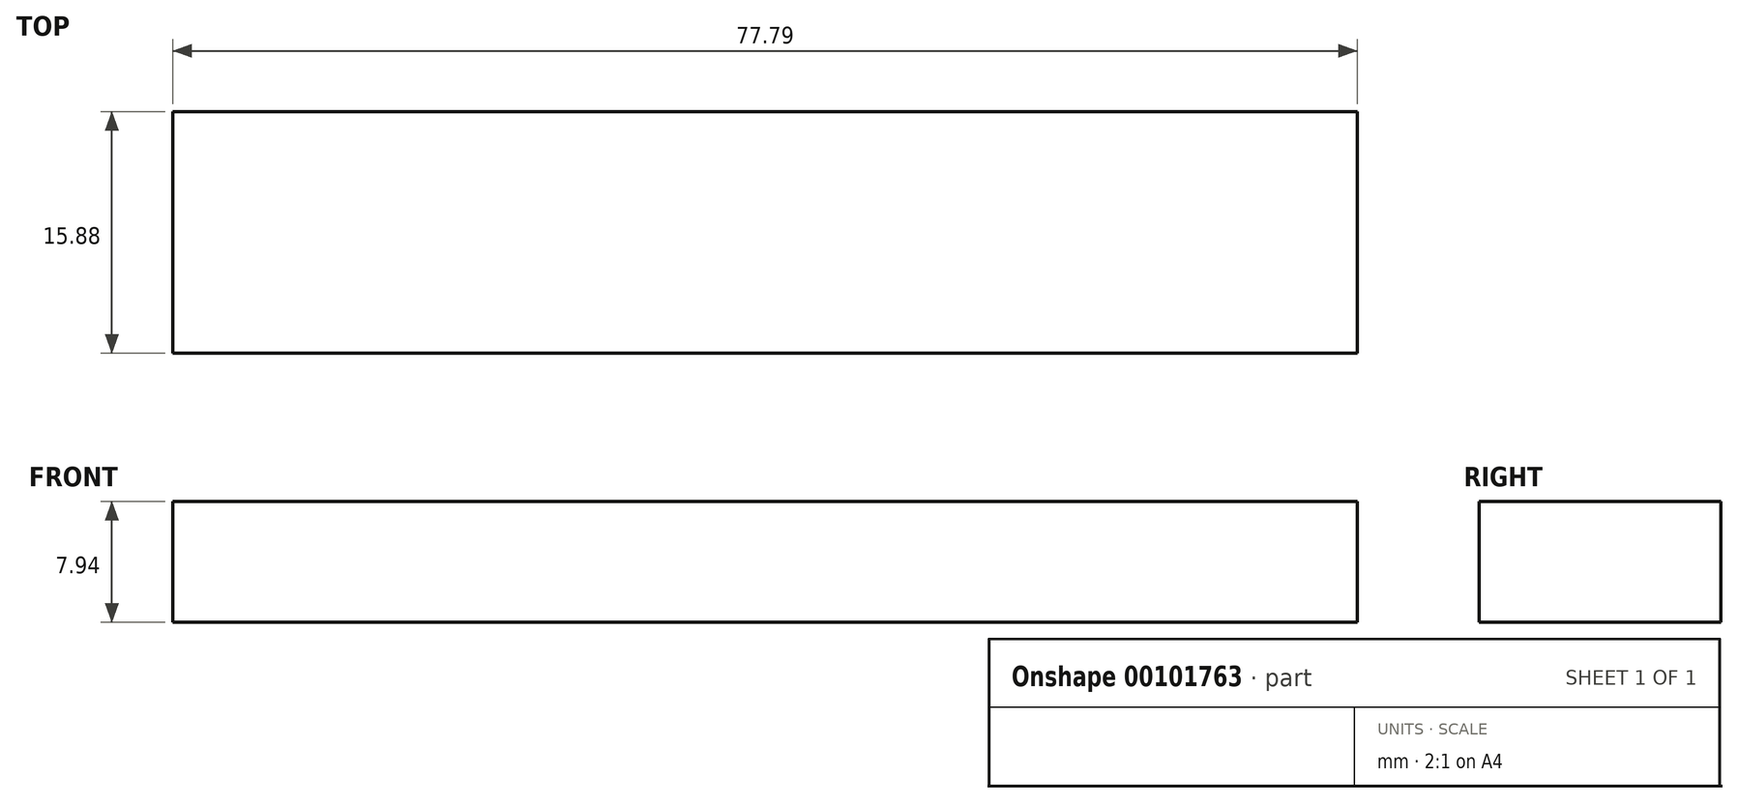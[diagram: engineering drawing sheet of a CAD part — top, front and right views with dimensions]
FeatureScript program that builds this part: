
annotation { "Feature Type Name" : "Feature", "Feature Type Description" : "" }
export const myFeature = defineFeature(function(context is Context, id is Id, definition is map)
    precondition{}
    {
        {
            var Q0;
            Q0=qCreatedBy(makeId("Front.planeOp"),FACE);
            var sketch = newSketch(context, id + "F0", { "sketchPlane" : qUnion([Q0])});
            skLineSegment(sketch, "E0.bottom", {"start": v(-51.57, 7.94) * mm, "end": v(26.22, 7.94) * mm});
            skLineSegment(sketch, "E0.top", {"start": v(-51.57, 0) * mm, "end": v(26.22, 0) * mm});
            skLineSegment(sketch, "E0.left", {"start": v(-51.57, 7.94) * mm, "end": v(-51.57, 0) * mm});
            skLineSegment(sketch, "E0.right", {"start": v(26.22, 7.94) * mm, "end": v(26.22, 0) * mm});
            skSolve(sketch);
        }
        {
            var Q0;
            Q0 = qSketchRegion(id + "F0", true);
            extrude(context, id + "F1", {"entities" : qUnion([Q0]), "depth" : 15.88 * mm});
        }
    });
